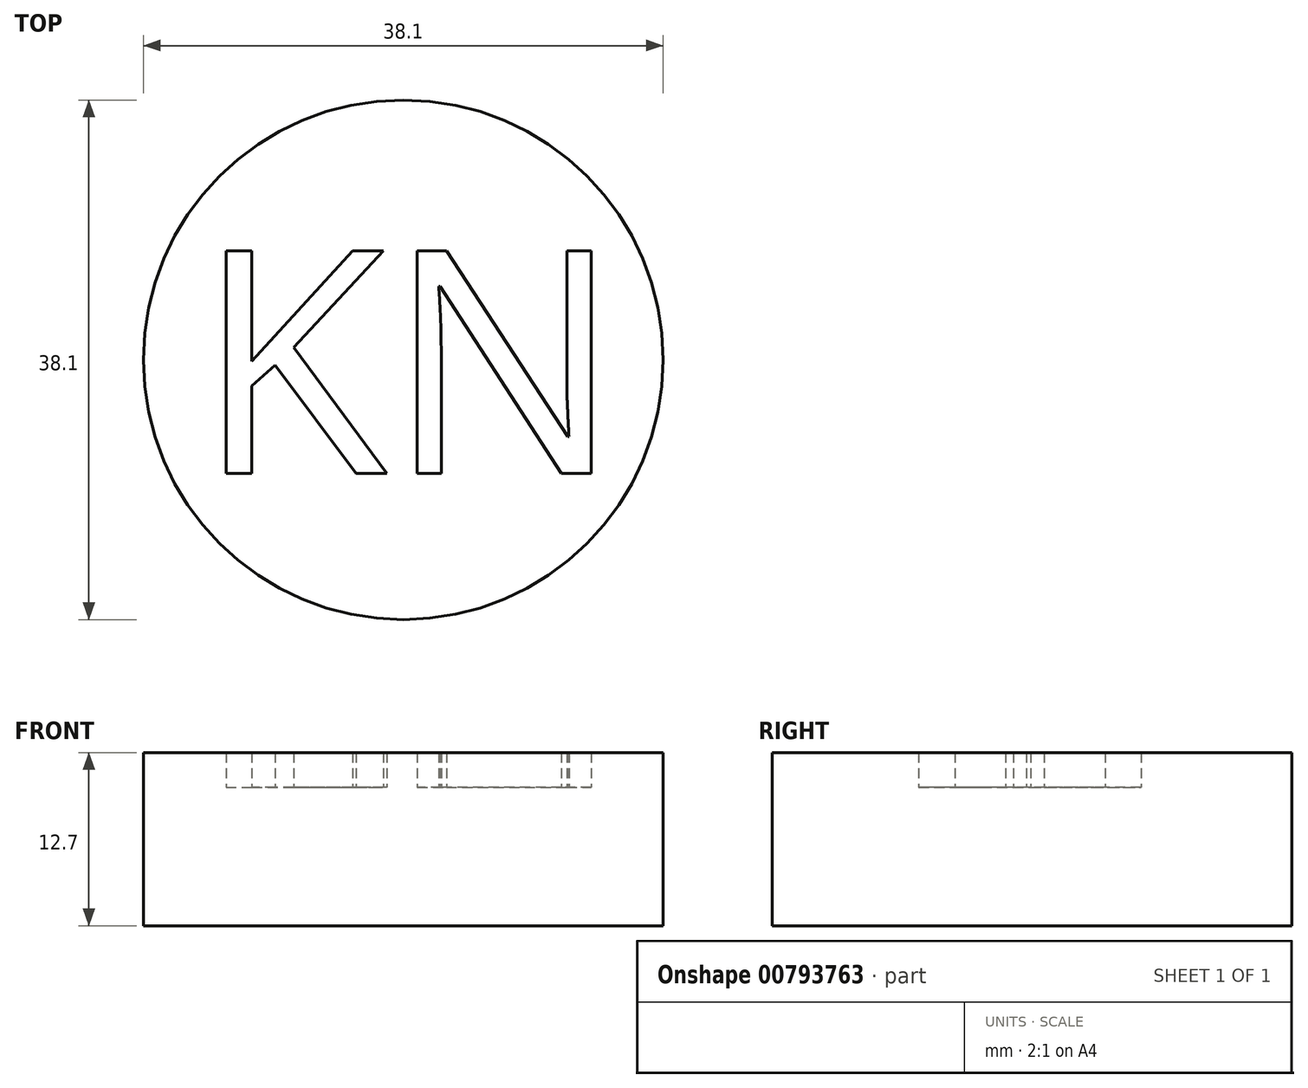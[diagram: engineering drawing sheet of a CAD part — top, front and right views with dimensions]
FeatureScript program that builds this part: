
annotation { "Feature Type Name" : "Feature", "Feature Type Description" : "" }
export const myFeature = defineFeature(function(context is Context, id is Id, definition is map)
    precondition{}
    {
        {
            var Q0;
            Q0=qCreatedBy(makeId("Top.planeOp"),FACE);
            var sketch = newSketch(context, id + "F0", { "sketchPlane" : qUnion([Q0])});
            skCircle(sketch, "E0", {"center": v(0, 0) * mm, "radius": 19.05 * mm});
            skSolve(sketch);
        }
        {
            var Q0;
            Q0=qCreatedBy(makeId("Top.planeOp"),FACE);
            var sketch = newSketch(context, id + "F1", { "sketchPlane" : qUnion([Q0])});
            skText(sketch, "E1", { "text": "KN", "fontName": "OpenSans-Regular.ttf"});
            const initialGuessF1  = {"E1": [-0.01524, -0.00832, 1, 0, 0.01645]};
            skSetInitialGuess(sketch, initialGuessF1);
            skSolve(sketch);
        }
        {
            var Q0;
            Q0 = qSketchRegion(id + "F0", true);
            extrude(context, id + "F2", {"entities" : qUnion([Q0]), "depth" : 12.7 * mm, "offsetDistance" : 25.4 * mm});
        }
        {
            var Q0;
            Q0 = qSketchRegion(id + "F1", true);
            extrude(context, id + "F3", {"entities" : qUnion([Q0]), "operationType" : NewBodyOperationType.REMOVE, "depth" : 12.7 * mm, "offsetDistance" : 25.4 * mm, "hasSecondDirection" : true, "secondDirectionOppositeDirection" : false, "secondDirectionDepth" : 10.16 * mm});
        }
    });
